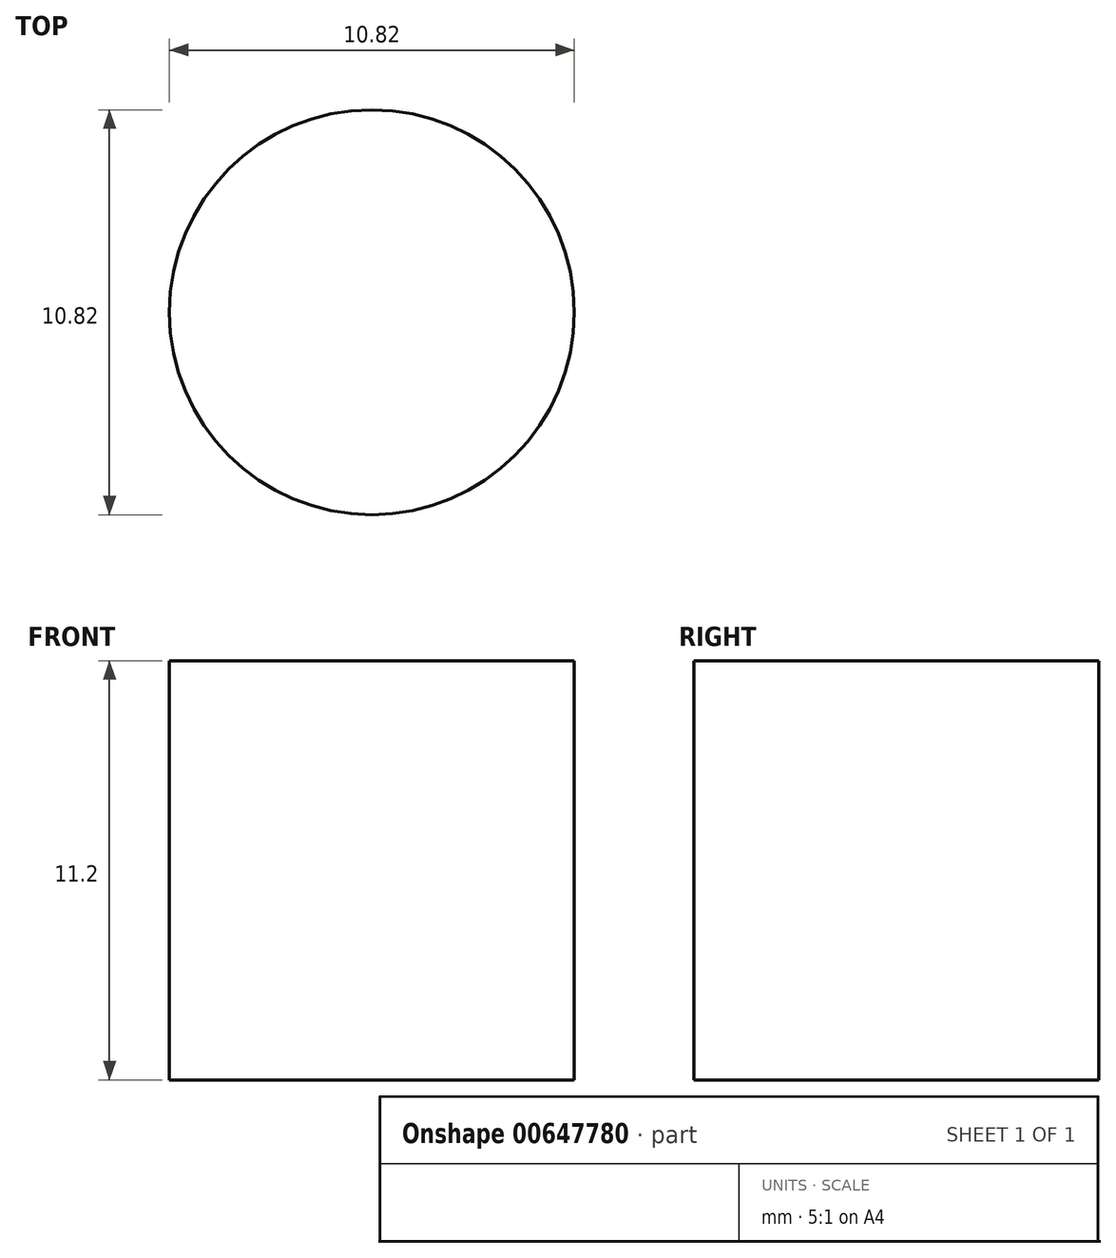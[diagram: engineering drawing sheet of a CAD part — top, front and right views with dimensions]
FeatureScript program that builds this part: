
annotation { "Feature Type Name" : "Feature", "Feature Type Description" : "" }
export const myFeature = defineFeature(function(context is Context, id is Id, definition is map)
    precondition{}
    {
        {
            var Q0;
            Q0=qCreatedBy(makeId("Top.planeOp"),FACE);
            var sketch = newSketch(context, id + "F0", { "sketchPlane" : qUnion([Q0])});
            skCircle(sketch, "E0", {"center": v(0, 0) * mm, "radius": 5.4 * mm});
            skSolve(sketch);
        }
        {
            var Q0;
            Q0=makeQuery(id+"F0.imprint","IMPRINT",FACE,{"disambiguationData":[TD([[makeQuery(id+"F0.imprint","IMPRINT",EDGE,{"derivedFrom":sQuery(id+"F0.wireOp",EDGE,"E0")}),1.0]])]});
            extrude(context, id + "F1", {"entities" : qUnion([Q0]), "depth" : 11.2 * mm, "offsetDistance" : 25 * mm});
        }
    });
